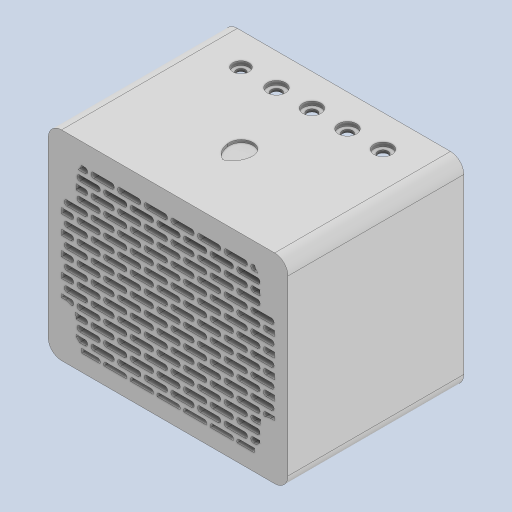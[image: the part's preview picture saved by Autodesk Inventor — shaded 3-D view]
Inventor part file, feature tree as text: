
AUTODESK INVENTOR PART (.ipt)
format: ipt  version: 2023 (Build 270158000, 158)  size: 2,521,088 bytes
history: native  units: mm
features: extrude x17, sketch x17, other x1
ambient origin geometry x8: Origin, YZ Plane, XZ Plane, XY Plane, X Axis, Y Axis, Z Axis, Center Point
bodies: Body1 (feature_tree)
feature tree (35):
  other  "Sólido1"
  extrude  "Extrusão1"  Depth=10.0mm
  extrude  "Extrusão2"  Depth=3.0mm
  extrude  "Extrusão3"  Depth=10.0mm
  extrude  "Extrusão4"  Depth=10.0mm
  extrude  "Extrusão5"  Depth=10.0mm
  extrude  "Extrusão6"  Depth=180.0mm
  extrude  "Extrusão7"  Depth=10.0mm
  extrude  "Extrusão8"  Depth=4.0mm TaperAngle=0.0deg
  extrude  "Extrusão9"  Depth=160.0mm
  sketch  "Esboço10"  dims[d49=10.0mm d50=2.5mm d51=3.0mm d52=2.5mm d53=4.0mm d54=128.0mm d55=0.0mm d56=0.0mm]
  extrude  "Extrusão10"  Depth=150.0mm
  extrude  "Extrusão11"  Depth=10.0mm
  extrude  "Extrusão12"  Depth=100.0mm
  extrude  "Extrusão13"  Depth=10.0mm
  extrude  "Extrusão14"  Depth=160.0mm
  extrude  "Extrusão15"  Depth=125.0mm
  extrude  "Extrusão17"  Depth=10.0mm
  extrude  "Extrusão18"  Depth=4.0mm TaperAngle=0.0deg
  sketch  "Esboço1"  dims[d4=10.0mm d8=2.5mm]
  sketch  "Esboço2"  dims[d12=3.0mm d13=2.5mm]
  sketch  "Esboço3"  dims[d14=4.0mm d15=0.0mm d16=10.0mm d17=2.5mm d18=3.0mm d19=2.5mm]
  sketch  "Esboço4"  dims[d20=10.0mm d21=0.0mm]
  sketch  "Esboço5"  dims[d22=10.0mm d23=2.5mm d24=3.0mm d25=2.5mm d26=5.0mm d27=0.0mm d28=10.0mm d29=2.5mm d30=3.0mm d31=2.5mm]
  sketch  "Esboço6"  dims[d32=70.0mm d33=0.0mm d34=10.0mm d35=2.5mm d36=3.0mm d37=2.5mm]
  sketch  "Esboço7"  dims[d38=7.0mm d39=0.0mm]
  sketch  "Esboço8"  dims[d40=10.0mm d41=2.5mm d42=3.0mm d43=2.5mm d44=45.0mm d45=0.0mm d46=180.0mm]
  sketch  "Esboço9"  dims[d47=150.0mm d48=10.0mm]
  sketch  "Esboço11"  dims[d64=128.0mm d65=0.0mm]
  sketch  "Esboço12"  dims[d66=6.0mm d67=45.0deg d68=2.0mm d71=6.0mm d72=0.0mm d73=160.0mm]
  sketch  "Esboço13"  dims[d74=98.0mm d75=150.0mm]
  sketch  "Esboço14"  dims[d76=125.0mm]
  sketch  "Esboço15"  dims[d77=6.0mm d78=45.0deg d79=2.0mm d80=160.0mm d81=98.0mm d82=150.0mm d83=125.0mm d86=10.0mm]
  sketch  "Esboço17"  dims[d87=70.0mm d89=20.0mm d90=30.0mm d92=20.0mm d95=100.0mm d97=14.0mm d98=10.0mm d100=10.0mm]
  sketch  "Esboço18"  dims[d102=10.0mm d103=2.5mm d104=3.0mm d105=2.5mm d106=10.0mm d107=2.5mm d108=3.0mm d109=2.5mm d110=160.0mm d111=125.0mm d112=10.0mm d113=4.0mm d114=0.0mm d115=4.0mm d116=0.0mm d117=87.0mm d118=90.0deg d119=3.0mm d120=90.0deg d121=21.0mm d122=26.67mm d123=90.0deg d124=26.67mm d125=26.67mm d126=180.0deg d127=26.67mm d128=180.0deg d129=26.67mm d130=180.0deg d131=26.67mm d132=180.0deg d135=6.5mm d136=7.5mm d137=7.5mm d138=7.5mm d139=7.5mm d141=7.0mm d142=0.0mm d143=13.5mm d144=13.5mm d145=13.5mm d146=13.5mm d147=3.0mm d148=0.0mm d149=12.0mm d150=46.0mm d151=90.0deg d152=84.0mm d153=90.0deg d154=19.0mm d155=90.0deg d156=34.33mm d157=22.0mm d158=34.33mm d159=35.0mm d160=180.0deg d161=34.33mm d162=180.0deg d163=20.0mm d164=13.0mm d165=20.8mm d166=12.8mm d167=3.0mm d168=90.0deg d169=25.5mm d170=90.0deg d171=10.0mm d172=65.0mm d173=20.0mm d174=12.0mm d175=5.0mm d176=45.0mm d177=4.0mm d178=7.0mm d179=5.0mm d180=0.0mm d181=46.0mm d182=90.0deg d183=84.0mm d184=90.0deg d185=19.0mm d186=90.0deg d187=34.33mm d188=22.0mm d189=34.33mm d190=35.0mm d191=180.0deg d192=34.33mm d193=180.0deg d194=20.0mm d195=13.0mm d196=20.8mm d197=12.8mm d198=3.0mm d199=90.0deg d200=25.5mm d201=90.0deg d202=10.0mm d203=65.0mm d204=20.0mm d205=12.0mm d206=5.0mm d207=45.0mm d208=4.0mm d209=7.0mm d210=27.5mm d211=1.0mm d212=2.0mm d213=2.0mm d214=58.0mm d215=1.0mm d216=2.0mm d217=2.0mm d218=5.0mm d219=0.0mm d222=14.0mm d223=12.0mm d224=3.0mm d225=0.0mm d226=19.471mm d227=23.44mm d228=1.5mm d229=2.0mm d230=0.0mm]
